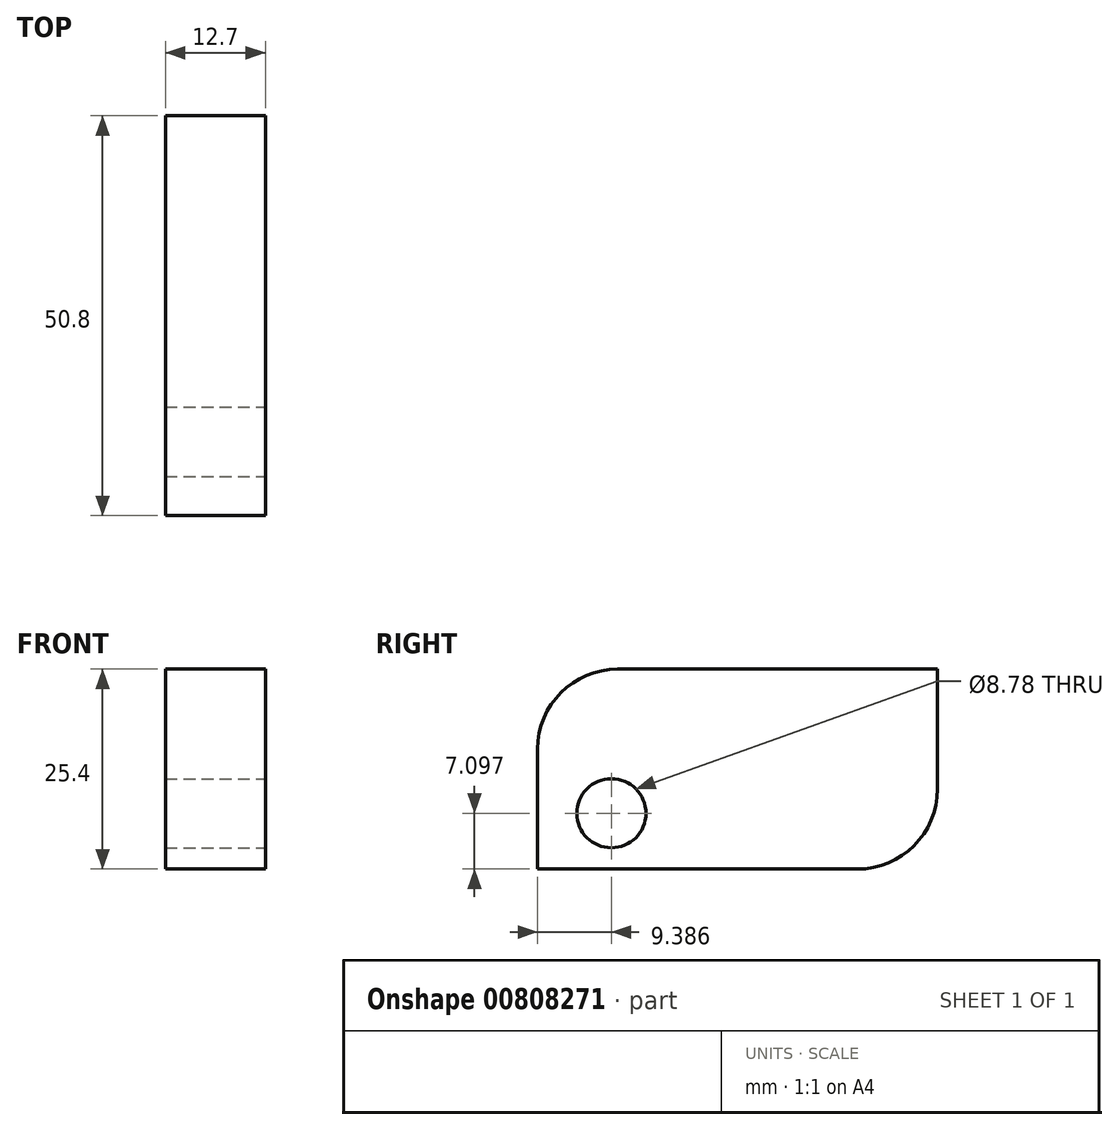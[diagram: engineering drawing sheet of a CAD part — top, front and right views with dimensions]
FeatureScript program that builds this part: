
annotation { "Feature Type Name" : "Feature", "Feature Type Description" : "" }
export const myFeature = defineFeature(function(context is Context, id is Id, definition is map)
    precondition{}
    {
        {
            var Q0;
            Q0=qCreatedBy(makeId("Right.planeOp"),FACE);
            var sketch = newSketch(context, id + "F0", { "sketchPlane" : qUnion([Q0])});
            skLineSegment(sketch, "E0.bottom", {"start": v(0, 0) * mm, "end": v(50.8, 0) * mm});
            skLineSegment(sketch, "E0.top", {"start": v(0, -25.4) * mm, "end": v(50.8, -25.4) * mm});
            skLineSegment(sketch, "E0.left", {"start": v(0, 0) * mm, "end": v(0, -25.4) * mm});
            skLineSegment(sketch, "E0.right", {"start": v(50.8, 0) * mm, "end": v(50.8, -25.4) * mm});
            skSolve(sketch);
        }
        {
            var Q0;
            Q0=makeQuery(id+"F0.imprint","IMPRINT",FACE,{"disambiguationData":[TD([[makeQuery(id+"F0.imprint","IMPRINT",EDGE,{"derivedFrom":sQuery(id+"F0.wireOp",EDGE,"E0.bottom")}),-1.0]])]});
            extrude(context, id + "F1", {"entities" : qUnion([Q0]), "depth" : 12.7 * mm, "offsetDistance" : 25.4 * mm});
        }
        {
            var Q0;
            Q0=makeQuery(id+"F1.opExtrude","SWEPT_EDGE",EDGE,{"disambiguationData":[OSD([sQuery(id+"F0.wireOp",EDGE,"E0.bottom"),sQuery(id+"F0.wireOp",EDGE,"E0.left")])]});
            var Q1;
            Q1=makeQuery(id+"F1.opExtrude","SWEPT_EDGE",EDGE,{"disambiguationData":[OSD([sQuery(id+"F0.wireOp",EDGE,"E0.top"),sQuery(id+"F0.wireOp",EDGE,"E0.right")])]});
            fillet(context, id + "F2", {"entities" : qUnion([Q0, Q1]), "radius" : 10.16 * mm, "tangentPropagation" : true, "allowEdgeOverflow" : false});
        }
        {
            var Q0;
            Q0=makeQuery(id+"F1.opExtrude","CAP_FACE",FACE,{"disambiguationData":[OSD([sQuery(id+"F0.wireOp",EDGE,"E0.bottom"),sQuery(id+"F0.wireOp",EDGE,"E0.top"),sQuery(id+"F0.wireOp",EDGE,"E0.left"),sQuery(id+"F0.wireOp",EDGE,"E0.right")])],"isStart":false});
            var sketch = newSketch(context, id + "F3", { "sketchPlane" : qUnion([Q0])});
            skCircle(sketch, "E1", {"center": v(9.39, -18.3) * mm, "radius": 4.39 * mm});
            skSolve(sketch);
        }
        {
            var Q0;
            Q0 = qSketchRegion(id + "F3", true);
            extrude(context, id + "F4", {"entities" : qUnion([Q0]), "operationType" : NewBodyOperationType.REMOVE, "oppositeDirection" : true, "depth" : 25.4 * mm, "offsetDistance" : 25.4 * mm});
        }
    });
